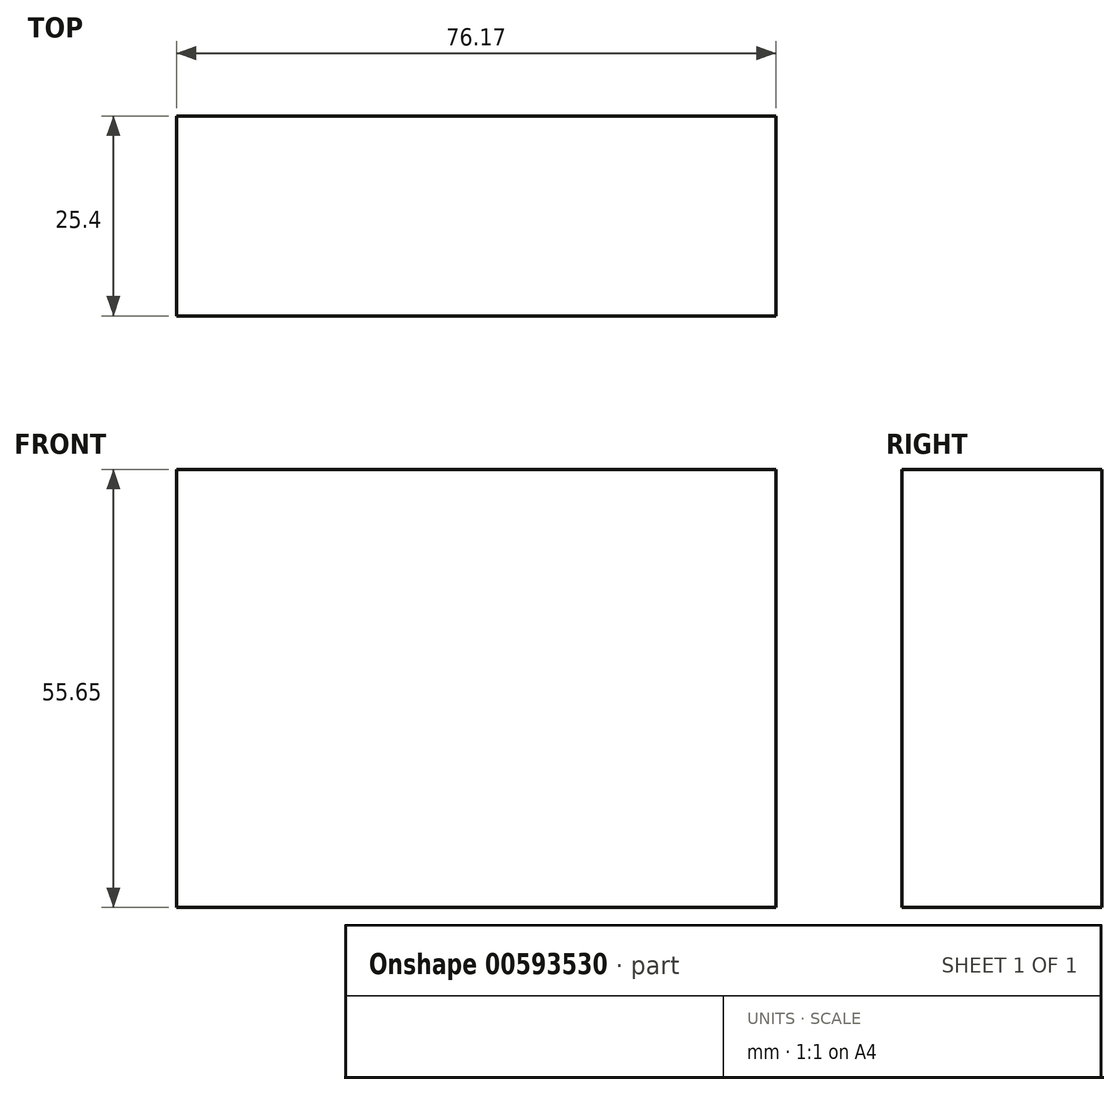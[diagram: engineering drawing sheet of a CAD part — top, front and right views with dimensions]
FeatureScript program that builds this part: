
annotation { "Feature Type Name" : "Feature", "Feature Type Description" : "" }
export const myFeature = defineFeature(function(context is Context, id is Id, definition is map)
    precondition{}
    {
        {
            var Q0;
            Q0=qCreatedBy(makeId("Front.planeOp"),FACE);
            var sketch = newSketch(context, id + "F0", { "sketchPlane" : qUnion([Q0])});
            skLineSegment(sketch, "E0.bottom", {"start": v(-109.08, 16.42) * mm, "end": v(-185.25, 16.42) * mm});
            skLineSegment(sketch, "E0.top", {"start": v(-109.08, 72.07) * mm, "end": v(-185.25, 72.07) * mm});
            skLineSegment(sketch, "E0.left", {"start": v(-109.08, 16.42) * mm, "end": v(-109.08, 72.07) * mm});
            skLineSegment(sketch, "E0.right", {"start": v(-185.25, 16.42) * mm, "end": v(-185.25, 72.07) * mm});
            skPoint(sketch, "E0.middle", {"position": v(-147.17, 44.24) * mm});
            skSolve(sketch);
        }
        {
            var Q0;
            Q0 = qSketchRegion(id + "F0", true);
            extrude(context, id + "F1", {"entities" : qUnion([Q0]), "depth" : 25.4 * mm, "offsetDistance" : 25.4 * mm});
        }
    });
